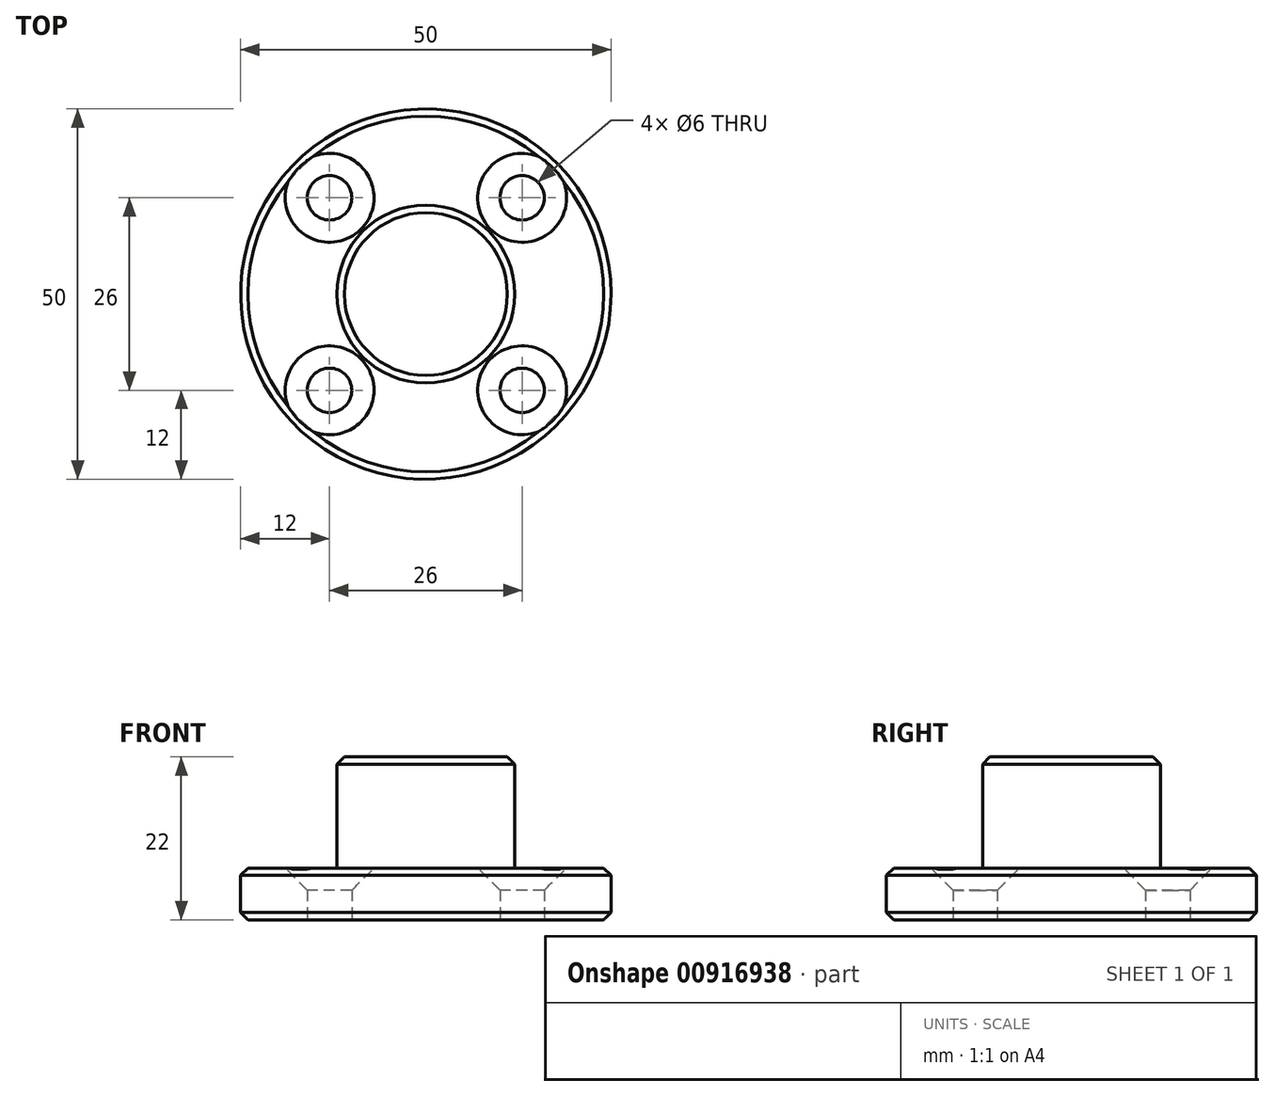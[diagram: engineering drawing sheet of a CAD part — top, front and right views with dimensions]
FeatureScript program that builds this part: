
annotation { "Feature Type Name" : "Feature", "Feature Type Description" : "" }
export const myFeature = defineFeature(function(context is Context, id is Id, definition is map)
    precondition{}
    {
        {
            var Q0;
            Q0=qCreatedBy(makeId("Top.planeOp"),FACE);
            var sketch = newSketch(context, id + "F0", { "sketchPlane" : qUnion([Q0])});
            skCircle(sketch, "E0", {"center": v(0, 0) * mm, "radius": 25 * mm});
            skCircle(sketch, "E1", {"center": v(-13, 13) * mm, "radius": 3 * mm});
            skCircle(sketch, "E2", {"center": v(13, 13) * mm, "radius": 3 * mm});
            skCircle(sketch, "E3", {"center": v(13, -13) * mm, "radius": 3 * mm});
            skCircle(sketch, "E4", {"center": v(-13, -13) * mm, "radius": 3 * mm});
            skSolve(sketch);
        }
        {
            var Q0;
            Q0=makeQuery(id+"F0.imprint","IMPRINT",FACE,{"disambiguationData":[TD([[makeQuery(id+"F0.imprint","IMPRINT",EDGE,{"derivedFrom":sQuery(id+"F0.wireOp",EDGE,"E0")}),1.0]])]});
            extrude(context, id + "F1", {"entities" : qUnion([Q0]), "depth" : 7 * mm, "offsetDistance" : 25 * mm});
        }
        {
            var Q0;
            Q0=makeQuery(id+"F1.opExtrude","CAP_FACE",FACE,{"disambiguationData":[OSD([sQuery(id+"F0.wireOp",EDGE,"E0"),sQuery(id+"F0.wireOp",EDGE,"E1"),sQuery(id+"F0.wireOp",EDGE,"E2"),sQuery(id+"F0.wireOp",EDGE,"E3"),sQuery(id+"F0.wireOp",EDGE,"E4")])],"isStart":false});
            var sketch = newSketch(context, id + "F2", { "sketchPlane" : qUnion([Q0])});
            skCircle(sketch, "E5", {"center": v(0, 0) * mm, "radius": 12 * mm});
            skSolve(sketch);
        }
        {
            var Q0;
            Q0=makeQuery(id+"F2.imprint","IMPRINT",FACE,{"disambiguationData":[TD([[makeQuery(id+"F2.imprint","IMPRINT",EDGE,{"derivedFrom":sQuery(id+"F2.wireOp",EDGE,"E5")}),1.0]])]});
            extrude(context, id + "F3", {"entities" : qUnion([Q0]), "operationType" : NewBodyOperationType.ADD, "depth" : 15 * mm, "offsetDistance" : 25 * mm});
        }
        {
            var Q0;
            Q0=makeQuery(id+"F3.opExtrude","CAP_EDGE",EDGE,{"disambiguationData":[OSD([sQuery(id+"F2.wireOp",EDGE,"E5")])],"isStart":false});
            var Q1;
            Q1=makeQuery(id+"F1.opExtrude","CAP_EDGE",EDGE,{"disambiguationData":[OSD([sQuery(id+"F0.wireOp",EDGE,"E0")])],"isStart":false});
            var Q2;
            Q2=makeQuery(id+"F1.opExtrude","CAP_EDGE",EDGE,{"disambiguationData":[OSD([sQuery(id+"F0.wireOp",EDGE,"E0")])],"isStart":true});
            chamfer(context, id + "F4", {"entities" : qUnion([Q0, Q1, Q2]), "width" : 1 * mm, "tangentPropagation" : true});
        }
        {
            var Q0;
            Q0=makeQuery(id+"F1.opExtrude","CAP_EDGE",EDGE,{"disambiguationData":[OSD([sQuery(id+"F0.wireOp",EDGE,"E4")])],"isStart":false});
            var Q1;
            Q1=makeQuery(id+"F1.opExtrude","CAP_EDGE",EDGE,{"disambiguationData":[OSD([sQuery(id+"F0.wireOp",EDGE,"E3")])],"isStart":false});
            var Q2;
            Q2=makeQuery(id+"F1.opExtrude","CAP_EDGE",EDGE,{"disambiguationData":[OSD([sQuery(id+"F0.wireOp",EDGE,"E2")])],"isStart":false});
            var Q3;
            Q3=makeQuery(id+"F1.opExtrude","CAP_EDGE",EDGE,{"disambiguationData":[OSD([sQuery(id+"F0.wireOp",EDGE,"E1")])],"isStart":false});
            chamfer(context, id + "F5", {"entities" : qUnion([Q0, Q1, Q2, Q3]), "chamferType" : ChamferType.TWO_OFFSETS, "width1" : 3 * mm, "oppositeDirection" : false, "width2" : 3 * mm, "tangentPropagation" : true});
        }
    });
